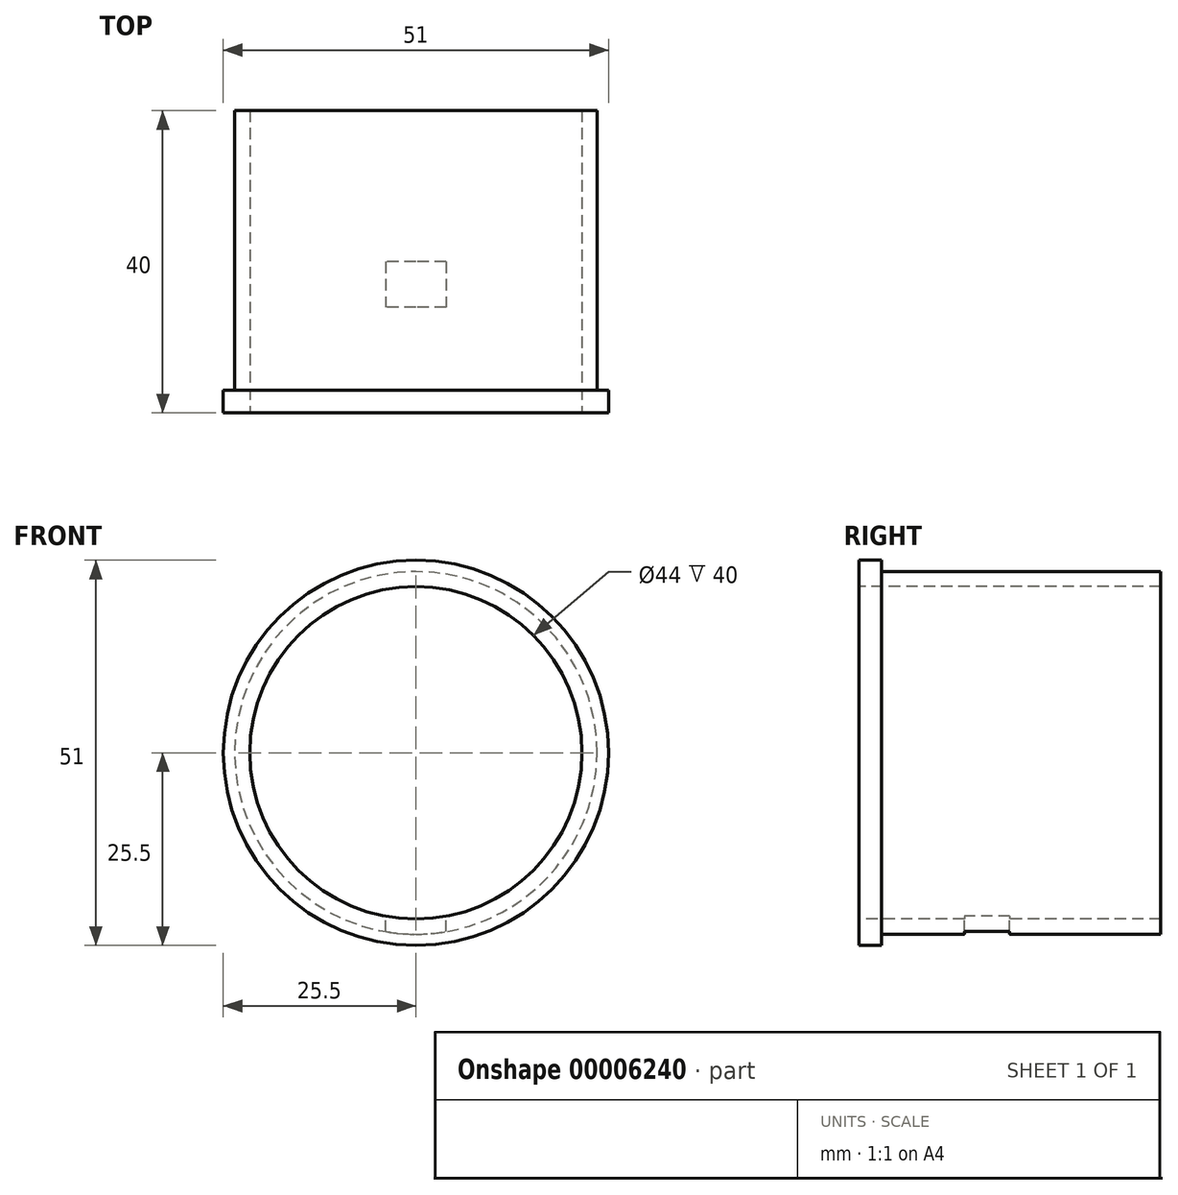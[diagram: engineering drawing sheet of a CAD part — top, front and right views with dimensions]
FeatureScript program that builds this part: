
annotation { "Feature Type Name" : "Feature", "Feature Type Description" : "" }
export const myFeature = defineFeature(function(context is Context, id is Id, definition is map)
    precondition{}
    {
        {
            var Q0;
            Q0=qCreatedBy(makeId("Right.planeOp"),FACE);
            var sketch = newSketch(context, id + "F0", { "sketchPlane" : qUnion([Q0])});
            skLineSegment(sketch, "E0", {"start": v(40, 24) * mm, "end": v(3, 24) * mm});
            skLineSegment(sketch, "E1", {"start": v(3, 24) * mm, "end": v(3, 25.5) * mm});
            skLineSegment(sketch, "E2", {"start": v(3, 25.5) * mm, "end": v(0, 25.5) * mm});
            skLineSegment(sketch, "E3", {"start": v(-35.86, 0) * mm, "end": v(48.8, 0) * mm, "construction": true});
            skLineSegment(sketch, "E4", {"start": v(0, 25.5) * mm, "end": v(0, 22) * mm});
            skLineSegment(sketch, "E5", {"start": v(0, 22) * mm, "end": v(40, 22) * mm});
            skLineSegment(sketch, "E6", {"start": v(40, 22) * mm, "end": v(40, 24) * mm});
            skSolve(sketch);
        }
        {
            var Q0;
            Q0=makeQuery(id+"F0.imprint","IMPRINT",FACE,{"disambiguationData":[TD([[makeQuery(id+"F0.imprint","IMPRINT",EDGE,{"derivedFrom":sQuery(id+"F0.wireOp",EDGE,"E0")}),1.0]])]});
            var Q1;
            Q1=sQuery(id+"F0.wireOp",EDGE,"E3");
            revolve(context, id + "F1", {"entities" : qUnion([Q0]), "axis" : qUnion([Q1]), "revolveType" : RevolveType.FULL});
        }
        {
            var Q0;
            Q0=qCreatedBy(makeId("Top.planeOp"),FACE);
            var sketch = newSketch(context, id + "F2", { "sketchPlane" : qUnion([Q0])});
            skLineSegment(sketch, "E7", {"start": v(0, -34.28) * mm, "end": v(0, 77.28) * mm, "construction": true});
            skLineSegment(sketch, "E8.rect.bottom", {"start": v(4, 14) * mm, "end": v(-4, 14) * mm});
            skLineSegment(sketch, "E8.rect.top", {"start": v(4, 20) * mm, "end": v(-4, 20) * mm});
            skLineSegment(sketch, "E8.rect.left", {"start": v(4, 14) * mm, "end": v(4, 20) * mm});
            skLineSegment(sketch, "E8.rect.right", {"start": v(-4, 14) * mm, "end": v(-4, 20) * mm});
            skPoint(sketch, "E8.rect.middle", {"position": v(0, 17) * mm});
            skSolve(sketch);
        }
        {
            var Q0;
            Q0=makeQuery(id+"F2.imprint","IMPRINT",FACE,{"disambiguationData":[TD([[makeQuery(id+"F2.imprint","IMPRINT",EDGE,{"derivedFrom":sQuery(id+"F2.wireOp",EDGE,"E8.rect.bottom")}),-1.0]])]});
            extrude(context, id + "F3", {"entities" : qUnion([Q0]), "operationType" : NewBodyOperationType.REMOVE, "endBound" : BoundingType.THROUGH_ALL, "oppositeDirection" : true, "depth" : 25 * mm});
        }
    });
